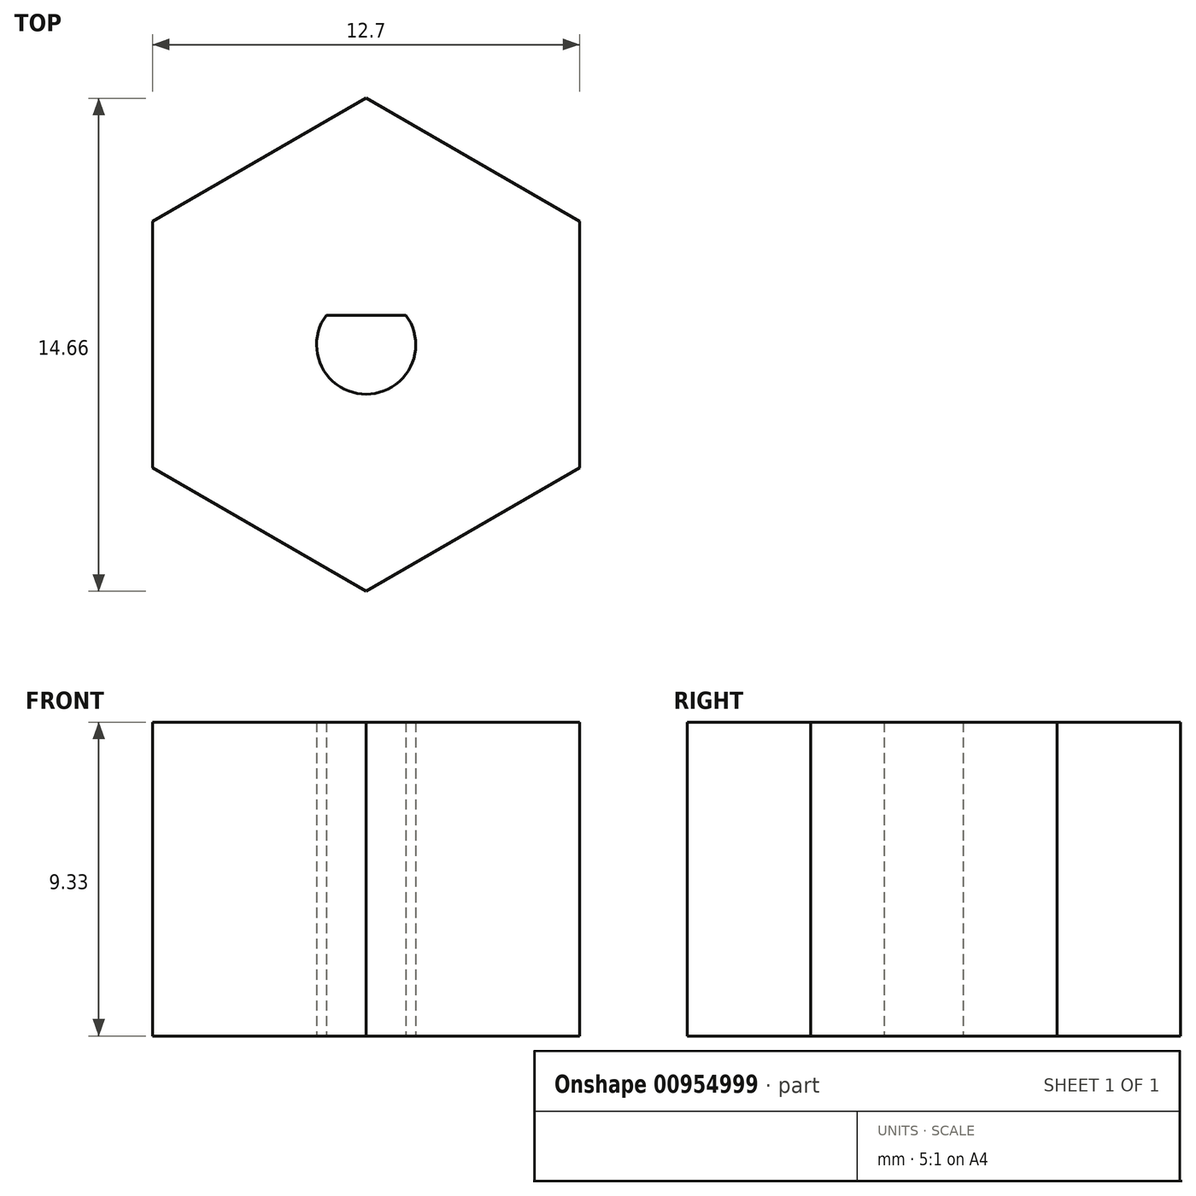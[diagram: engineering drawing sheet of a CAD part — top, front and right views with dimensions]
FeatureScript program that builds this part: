
annotation { "Feature Type Name" : "Feature", "Feature Type Description" : "" }
export const myFeature = defineFeature(function(context is Context, id is Id, definition is map)
    precondition{}
    {
        {
            var Q0;
            Q0=qCreatedBy(makeId("Top.planeOp"),FACE);
            var sketch = newSketch(context, id + "F0", { "sketchPlane" : qUnion([Q0])});
            skCircle(sketch, "E0.cCircle", {"center": v(0, 0) * mm, "radius": 6.35 * mm, "construction": true});
            skLineSegment(sketch, "E0.0", {"start": v(0, 7.33) * mm, "end": v(6.35, 3.67) * mm});
            skLineSegment(sketch, "E0.1", {"start": v(6.35, 3.67) * mm, "end": v(6.35, -3.67) * mm});
            skLineSegment(sketch, "E0.2", {"start": v(6.35, -3.67) * mm, "end": v(0, -7.33) * mm});
            skLineSegment(sketch, "E0.3", {"start": v(0, -7.33) * mm, "end": v(-6.35, -3.67) * mm});
            skLineSegment(sketch, "E0.4", {"start": v(-6.35, -3.67) * mm, "end": v(-6.35, 3.67) * mm});
            skLineSegment(sketch, "E0.5", {"start": v(-6.35, 3.67) * mm, "end": v(0, 7.33) * mm});
            skPoint(sketch, "E0.0.midPoint", {"position": v(3.17, 5.5) * mm});
            skCircle(sketch, "E1", {"center": v(0, 0) * mm, "radius": 1.47 * mm, "construction": true});
            skArc(sketch, "E2", {"start": v(-1.18, 0.88) * mm, "mid": v(0, -1.47) * mm, "end": v(1.18, 0.88) * mm});
            skPoint(sketch, "E3", {"position": v(0, -1.47) * mm});
            skLineSegment(sketch, "E4", {"start": v(-1.18, 0.88) * mm, "end": v(1.18, 0.88) * mm});
            skSolve(sketch);
        }
        {
            var Q0;
            Q0 = qSketchRegion(id + "F0", true);
            extrude(context, id + "F1", {"entities" : qUnion([Q0]), "depth" : 9.33 * mm, "offsetDistance" : 25.4 * mm});
        }
    });
